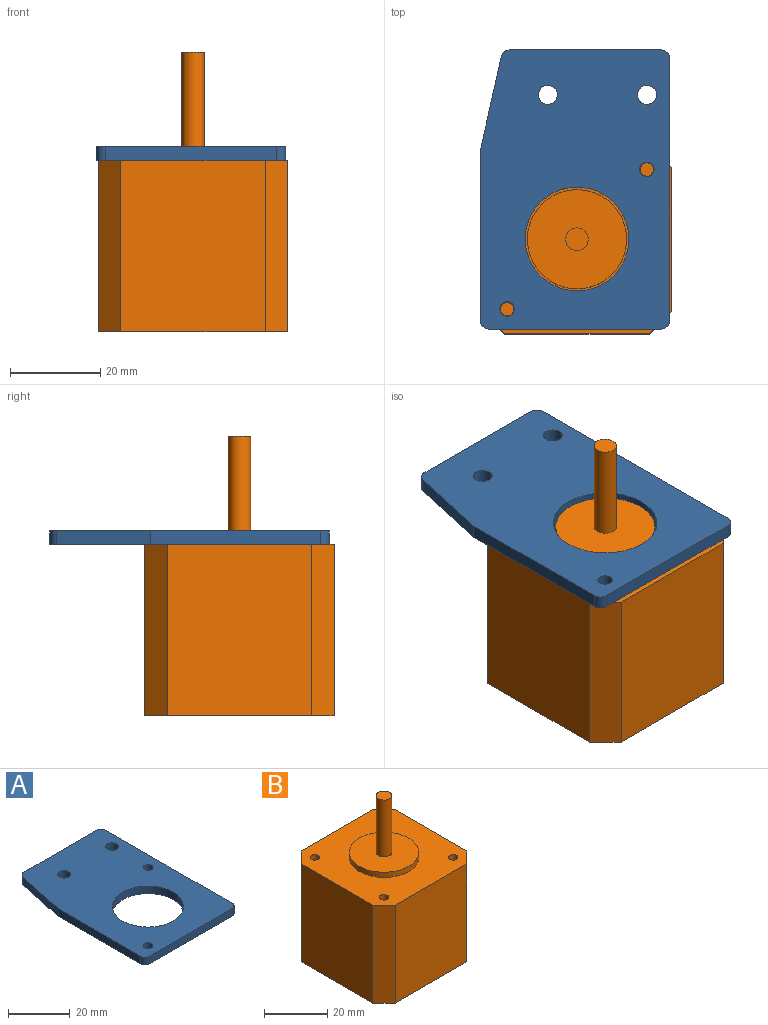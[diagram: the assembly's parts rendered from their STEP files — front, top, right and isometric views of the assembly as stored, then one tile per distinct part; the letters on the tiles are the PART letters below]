
ASSEMBLY  parts=2 mates=1
PART A: 16 faces, bbox 42x62x3 mm
  f0: plane 58x3mm, normal (1,0,0), area 174mm2, adj f1,f13,f14,f15
  f1: cylinder r=2mm len=3mm, axis (0,0,-1), area 9.4mm2, adj f0,f2,f14,f15
  f2: plane 38x3mm, normal (0,-1,0), area 114mm2, adj f1,f3,f14,f15
  f3: cylinder r=2mm len=3mm, axis (0,0,-1), area 9.4mm2, adj f2,f4,f14,f15
  f4: plane 37.74x3mm, normal (-1,0,0), area 113.2mm2, adj f3,f5,f14,f15
  f5: plane 20.7x4.65mm, normal (-0.98,0.22,0), area 63.6mm2, adj f4,f6,f14,f15
  f6: cylinder r=2mm len=3mm, axis (0,0,-1), area 8.1mm2, adj f5,f7,f14,f15
  f7: plane 33.4x3mm, normal (0,1,0), area 100.2mm2, adj f6,f13,f14,f15
  f8: cylinder r=11.5mm len=23mm, axis (0,0,-1), area 216.8mm2, adj f14,f15
  f9: cylinder r=1.6mm len=3.2mm, axis (0,0,-1), area 30.2mm2, adj f14,f15
  f10: cylinder r=1.6mm len=3.2mm, axis (0,0,-1), area 30.2mm2, adj f14,f15
  f11: cylinder r=2.1mm len=4.2mm, axis (0,0,-1), area 39.6mm2, adj f14,f15
  f12: cylinder r=2.1mm len=4.2mm, axis (0,0,-1), area 39.6mm2, adj f14,f15
  f13: cylinder r=2mm len=3mm, axis (0,0,-1), area 9.4mm2, adj f0,f7,f14,f15
  f14: plane 62x42mm, normal (0,0,1), area 2086mm2, adj f0,f1,f2,f3,f4,f5,f6,f7
  f15: plane 62x42mm, normal (0,0,-1), area 2086mm2, adj f0,f1,f2,f3,f4,f5,f6,f7
PART B: 22 faces, bbox 42x42x62 mm
  f0: plane 38x32mm, normal (-1,0,0), area 1216mm2, adj f4,f5,f8,f9
  f1: plane 38x32mm, normal (0,-1,0), area 1216mm2, adj f4,f5,f7,f9
  f2: plane 38x32mm, normal (1,0,0), area 1216mm2, adj f4,f5,f6,f7
  f3: plane 38x32mm, normal (0,1,0), area 1216mm2, adj f4,f5,f6,f8
  f4: plane 42x42mm, normal (0,0,1), area 1305.6mm2, adj f0,f1,f2,f3,f6,f7,f8,f9
  f5: plane 42x42mm, normal (0,0,-1), area 1714mm2, adj f0,f1,f2,f3,f6,f7,f8,f9
  f6: plane 38x5mm, normal (0.71,0.71,0), area 268.7mm2, adj f2,f3,f4,f5
  f7: plane 38x5mm, normal (0.71,-0.71,0), area 268.7mm2, adj f1,f2,f4,f5
  f8: plane 38x5mm, normal (-0.71,0.71,0), area 268.7mm2, adj f0,f3,f4,f5
  f9: plane 38x5mm, normal (-0.71,-0.71,0), area 268.7mm2, adj f0,f1,f4,f5
  f10: cylinder r=11mm len=22mm, axis (0,0,-1), area 138.2mm2, adj f4,f11
  f11: plane 22x22mm, normal (0,0,1), area 360.5mm2, adj f10,f12
  f12: cylinder r=2.5mm len=22mm, axis (0,0,-1), area 345.6mm2, adj f11,f13
  f13: plane 5x5mm, normal (0,0,1), area 19.6mm2, adj f12
  f14: cylinder r=1.5mm len=25mm, axis (0,0,1), area 235.6mm2, adj f4,f15
  f15: plane 3x3mm, normal (0,0,1), area 7.1mm2, adj f14
  f16: cylinder r=1.5mm len=25mm, axis (0,0,1), area 235.6mm2, adj f4,f17
  f17: plane 3x3mm, normal (0,0,1), area 7.1mm2, adj f16
  f18: cylinder r=1.5mm len=25mm, axis (0,0,1), area 235.6mm2, adj f4,f19
  f19: plane 3x3mm, normal (0,0,1), area 7.1mm2, adj f18
  f20: cylinder r=1.5mm len=25mm, axis (0,0,1), area 235.6mm2, adj f4,f21
  f21: plane 3x3mm, normal (0,0,1), area 7.1mm2, adj f20
PLACE A at identity
PLACE B rot(axis=(0,0,-1),90deg) t=(-20.87,-7.47,-38)mm
MATE fastened B.f20 <-> A.f10  axis (0,0,1) through (15.63,-12.97,0)mm
